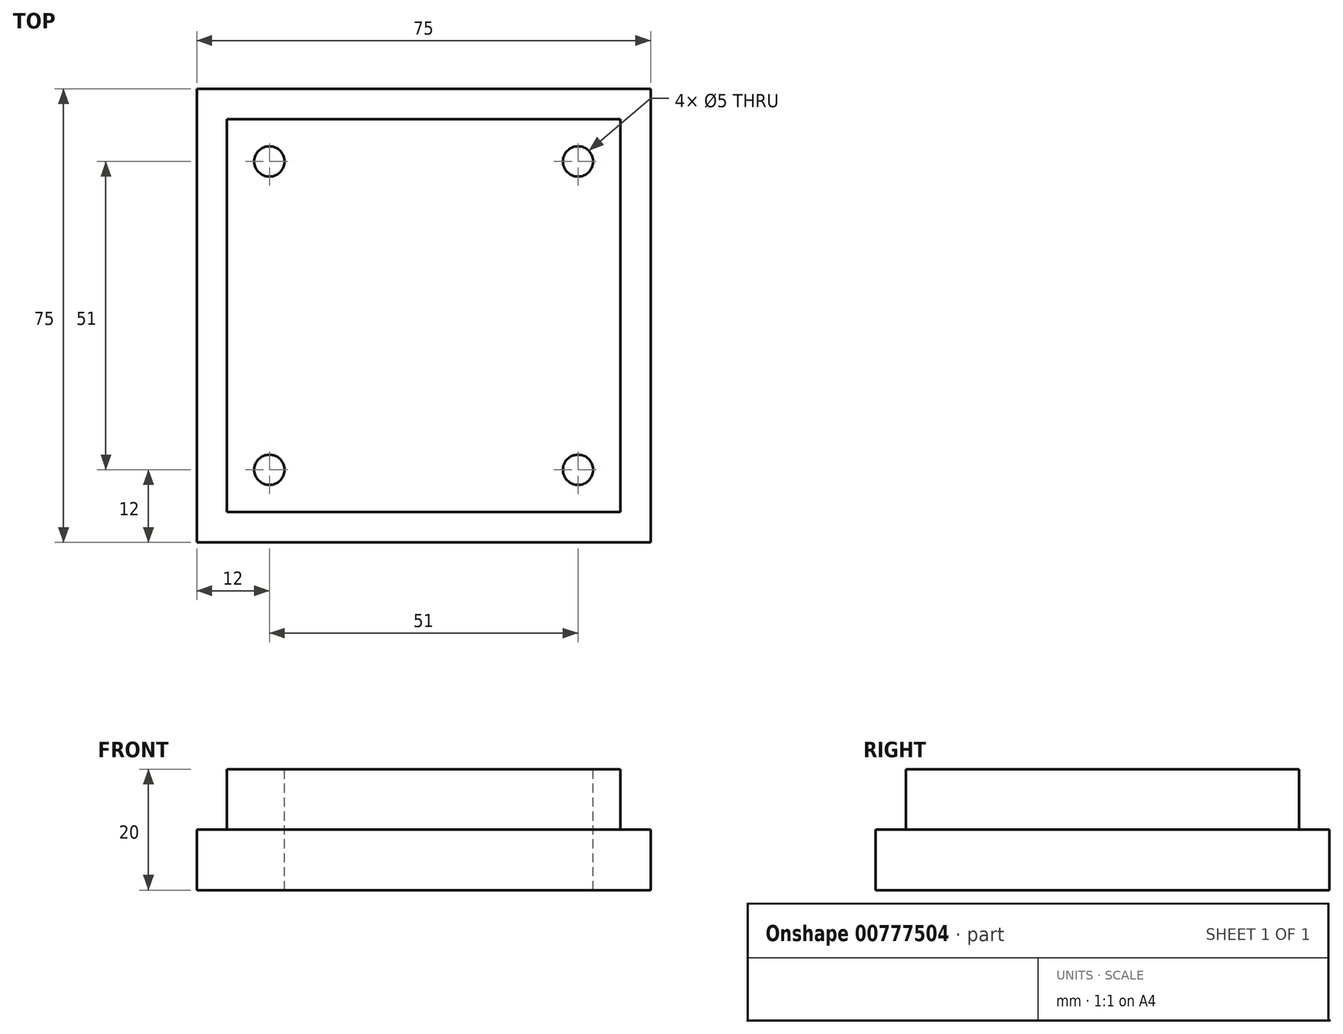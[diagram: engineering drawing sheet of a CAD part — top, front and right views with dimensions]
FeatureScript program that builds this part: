
annotation { "Feature Type Name" : "Feature", "Feature Type Description" : "" }
export const myFeature = defineFeature(function(context is Context, id is Id, definition is map)
    precondition{}
    {
        {
            var Q0;
            Q0=qCreatedBy(makeId("Top.planeOp"),FACE);
            var sketch = newSketch(context, id + "F0", { "sketchPlane" : qUnion([Q0])});
            skLineSegment(sketch, "E0.bottom", {"start": v(-37.5, 37.5) * mm, "end": v(37.5, 37.5) * mm});
            skLineSegment(sketch, "E0.top", {"start": v(-37.5, -37.5) * mm, "end": v(37.5, -37.5) * mm});
            skLineSegment(sketch, "E0.left", {"start": v(-37.5, 37.5) * mm, "end": v(-37.5, -37.5) * mm});
            skLineSegment(sketch, "E0.right", {"start": v(37.5, 37.5) * mm, "end": v(37.5, -37.5) * mm});
            skPoint(sketch, "E0.middle", {"position": v(0, 0) * mm});
            skSolve(sketch);
        }
        {
            var Q0;
            Q0 = qSketchRegion(id + "F0", true);
            extrude(context, id + "F1", {"entities" : qUnion([Q0]), "depth" : 10 * mm, "offsetDistance" : 25 * mm});
        }
        {
            var Q0;
            Q0=makeQuery(id+"F1.opExtrude","CAP_FACE",FACE,{"disambiguationData":[OSD([sQuery(id+"F0.wireOp",EDGE,"E0.bottom"),sQuery(id+"F0.wireOp",EDGE,"E0.top"),sQuery(id+"F0.wireOp",EDGE,"E0.left"),sQuery(id+"F0.wireOp",EDGE,"E0.right")])],"isStart":false});
            var sketch = newSketch(context, id + "F2", { "sketchPlane" : qUnion([Q0])});
            skLineSegment(sketch, "E1.bottom", {"start": v(-32.5, 32.5) * mm, "end": v(32.5, 32.5) * mm});
            skLineSegment(sketch, "E1.top", {"start": v(-32.5, -32.5) * mm, "end": v(32.5, -32.5) * mm});
            skLineSegment(sketch, "E1.left", {"start": v(-32.5, 32.5) * mm, "end": v(-32.5, -32.5) * mm});
            skLineSegment(sketch, "E1.right", {"start": v(32.5, 32.5) * mm, "end": v(32.5, -32.5) * mm});
            skPoint(sketch, "E1.middle", {"position": v(0, 0) * mm});
            skSolve(sketch);
        }
        {
            var Q0;
            Q0 = qSketchRegion(id + "F2", true);
            extrude(context, id + "F3", {"entities" : qUnion([Q0]), "operationType" : NewBodyOperationType.ADD, "depth" : 10 * mm, "offsetDistance" : 25 * mm});
        }
        {
            var Q0;
            Q0=makeQuery(id+"F3.opExtrude","CAP_FACE",FACE,{"disambiguationData":[OSD([sQuery(id+"F2.wireOp",EDGE,"E1.bottom"),sQuery(id+"F2.wireOp",EDGE,"E1.top"),sQuery(id+"F2.wireOp",EDGE,"E1.left"),sQuery(id+"F2.wireOp",EDGE,"E1.right")])],"isStart":false});
            var sketch = newSketch(context, id + "F4", { "sketchPlane" : qUnion([Q0])});
            skCircle(sketch, "E2", {"center": v(-25.5, 25.5) * mm, "radius": 2.5 * mm});
            skCircle(sketch, "E3", {"center": v(25.5, 25.5) * mm, "radius": 2.5 * mm});
            skCircle(sketch, "E4", {"center": v(25.5, -25.5) * mm, "radius": 2.5 * mm});
            skCircle(sketch, "E5", {"center": v(-25.5, -25.5) * mm, "radius": 2.5 * mm});
            skSolve(sketch);
        }
        {
            var Q0;
            Q0 = qSketchRegion(id + "F4", true);
            extrude(context, id + "F5", {"entities" : qUnion([Q0]), "operationType" : NewBodyOperationType.REMOVE, "endBound" : BoundingType.THROUGH_ALL, "oppositeDirection" : true, "depth" : 25 * mm, "offsetDistance" : 25 * mm});
        }
    });
